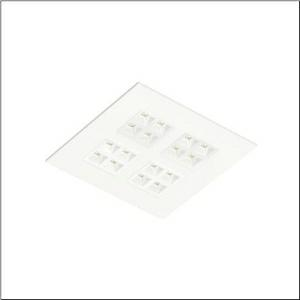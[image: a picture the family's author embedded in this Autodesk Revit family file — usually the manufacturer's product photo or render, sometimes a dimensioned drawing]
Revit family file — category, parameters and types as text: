
# Revit family: silica_r__31_square_51my6nms44wa_aede
name_source: partatom
category: Lighting Fixtures
units: mm (PartAtom-declared; Revit-internal decimal feet)

## family parameters
Cut with Voids When Loaded = No
Host = Face
Light Source = No
Part Type = Normal
Room Calculation Point = No
Round Connector Dimension = Use Diameter
Shared = No

## types (1)
- --- (1 x LED, 6970 lm, 39 W, 4000K)
    Apparent Load = 39 VA
    CIE Flux Codes = 81 99 100 100 100
    Color Rendering = 80
    Color Temperature = 4000K
    Default Elevation = 1800 mm
    Description = Silica® 31 Square, office luminaire, primary light control with lens, of PMMA, primary anti-glare with reflector, of PC, white, light emission: direct distribution, primary light characteristic: symmetric, installation type: lay-in mounting, LED, rated luminous flux: 4.560lm, luminous efficacy: 186lm/W, light colour: 840, colour temperature: 4000K, control gear: ON/OFF Multilumen, with terminal, 3-pole, mains connection: 220..240V, AC, 50/60Hz, rated input power: 24.5W, luminaire housing, of sheet steel, coated, traffic white (RAL 9016), module: M600, length: 595mm, width: 595mm, height: 43mm, protection rating (complete): IP20, insulation class (complete): insulation class II (safety insulation), certification: CE, impact resistance: IK03, permissible operating ambient temperature: -20..+35°C, standard: EN 50419, packaging unit: 1 piece
    Height = 0 mm  [stored 0 ft]
    Lamp = 1 x LED
    Lamp Light Flux = 6970 lm
    Lamp Power = 39 W
    Lamp count = 1
    Length = 595 mm
    Luminous efficacy = 179 lm/W
    Manufacturer = Siteco
    ModVariant = No
    Model = 51MY6NMS44WA
    Mounting Place = Ceiling
    Mounting Type = Recessed
    Number of Poles = 1
    OnlyDefault = Yes
    Power Factor = 1
    Product Name = Silica® 31 Square
    Product group = office luminaire | ceiling recessed
    ProductGroupID = 401
    Protection Class = Protection class II
    Protection Degree = IP 20
    RLX_Detail_Level = 1
    RLX_Emergency_Light_Flux = 0 lm
    RLX_Emergency_Type = 0
    RLX_Emergency_Type_DB = No
    RlxData = <blob elided: 28489 chars, md5=f7d11ca4>
    Socket = socket
    Standby Power = 0 W
    System Light Flux = 6970 lm
    System Power = 39 W
    Type Comments = factory setting: luminous flux: 100 % | (ON | ON | ON | ON) | 1100 mA
    Type Image = l_1313651.jpg
    URL = http://relux.com
    VarID = @adj_036020
    Voltage = 0 V
    Weight = 0.00 kg
    Width = 595 mm

note: [stored X ft] marks values corroborated as IEEE doubles in the binary element streams (Revit-internal decimal feet)

## geometry (parser evidence)
native form markers: Blend x4, Sweep x10
no freeform markers — native parametric forms only
